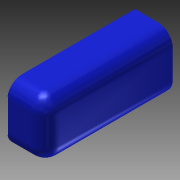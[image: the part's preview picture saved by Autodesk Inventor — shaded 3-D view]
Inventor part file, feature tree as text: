
AUTODESK INVENTOR PART (.ipt)
format: ipt  version: 2013 (Build 170138000, 138)  size: 183,808 bytes
history: native  units: in
note: dims shown in document units (in); Inventor stores cm internally (conversion verified against a paired STEP export)
features: reference x4, extrude x3, sketch x2, fillet x1, projected_geometry x1
ambient origin geometry x8: Origin, YZ Plane, XZ Plane, XY Plane, X Axis, Y Axis, Z Axis, Center Point
bodies: Solid1 (feature_tree)
feature tree (11):
  sketch  "Sketch1"  dims[d0=0.0625in d1=0.0in d3=1.0in]
  extrude  "Extrusion1"  Depth=1.0in
  extrude  "Extrusion2"  Depth=0.0625in
  extrude  "Extrusion3"  Depth=11.25in TaperAngle=0.0deg
  fillet  "Fillet1"  Radius=0.0625in
  reference  "Reference4"
  reference  "Reference5"
  sketch  "Sketch2"  dims[d7=1.0in d9=0.0625in d10=11.25in d11=0.0in d12=0.0625in d13=0.0in d14=1.3125in d15=0.0625in d16=0.0625in]
  reference  "Reference6"
  projected_geometry  "Projected Loop1"
  reference  "Reference7"
